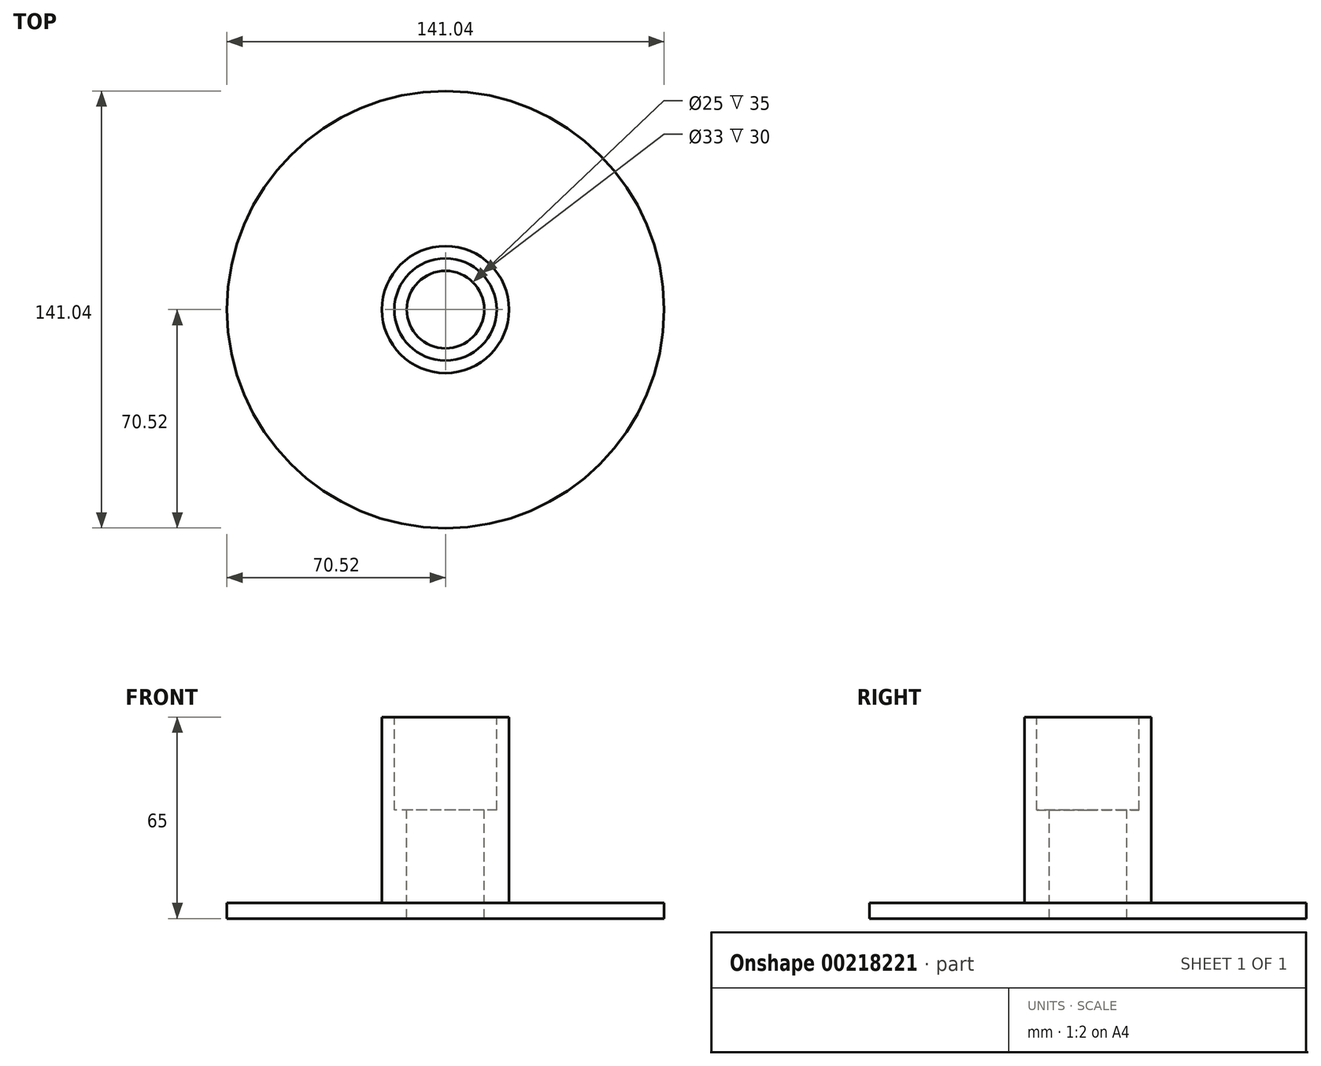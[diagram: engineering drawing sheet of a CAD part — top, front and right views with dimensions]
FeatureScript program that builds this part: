
annotation { "Feature Type Name" : "Feature", "Feature Type Description" : "" }
export const myFeature = defineFeature(function(context is Context, id is Id, definition is map)
    precondition{}
    {
        {
            var Q0;
            Q0=qCreatedBy(makeId("Front.planeOp"),FACE);
            var sketch = newSketch(context, id + "F0", { "sketchPlane" : qUnion([Q0])});
            skLineSegment(sketch, "E0.bottom", {"start": v(71.48, 6.77) * mm, "end": v(-70.52, 6.77) * mm});
            skLineSegment(sketch, "E0.top", {"start": v(71.48, 1.77) * mm, "end": v(-70.52, 1.77) * mm});
            skLineSegment(sketch, "E0.left", {"start": v(71.48, 6.77) * mm, "end": v(71.48, 1.77) * mm});
            skLineSegment(sketch, "E0.right", {"start": v(-70.52, 6.77) * mm, "end": v(-70.52, 1.77) * mm});
            skLineSegment(sketch, "E1.top", {"start": v(20.5, 66.77) * mm, "end": v(-20.5, 66.77) * mm});
            skLineSegment(sketch, "E1.left", {"start": v(20.5, 6.77) * mm, "end": v(20.5, 66.77) * mm});
            skLineSegment(sketch, "E1.right", {"start": v(-20.5, 6.77) * mm, "end": v(-20.5, 66.77) * mm});
            skPoint(sketch, "E1.middle", {"position": v(0, 36.77) * mm});
            skLineSegment(sketch, "E2", {"start": v(-12.5, 66.77) * mm, "end": v(-12.5, 6.77) * mm});
            skLineSegment(sketch, "E3.MirrorCS", {"start": v(12.5, 66.77) * mm, "end": v(12.5, 6.77) * mm});
            skLineSegment(sketch, "E4", {"start": v(-16.5, 66.77) * mm, "end": v(-16.5, 36.77) * mm});
            skLineSegment(sketch, "E5", {"start": v(-16.5, 36.77) * mm, "end": v(-20.5, 36.77) * mm});
            skLineSegment(sketch, "E6.MirrorCS", {"start": v(16.5, 36.77) * mm, "end": v(20.5, 36.77) * mm});
            skLineSegment(sketch, "E7.MirrorCS", {"start": v(16.5, 66.77) * mm, "end": v(16.5, 36.77) * mm});
            skLineSegment(sketch, "E8", {"start": v(-16.5, 36.77) * mm, "end": v(-12.5, 36.77) * mm});
            skLineSegment(sketch, "E9.MirrorCS", {"start": v(16.5, 36.77) * mm, "end": v(12.5, 36.77) * mm});
            skLineSegment(sketch, "E10", {"start": v(-12.5, 6.77) * mm, "end": v(-12.5, 1.77) * mm});
            skLineSegment(sketch, "E11.MirrorCS", {"start": v(12.5, 6.77) * mm, "end": v(12.5, 1.77) * mm});
            skLineSegment(sketch, "E12", {"start": v(0, 81.08) * mm, "end": v(0, -48.61) * mm, "construction": true});
            skSolve(sketch);
        }
        {
            var Q0;
            {var subQ0=sQuery(id+"F0.wireOp",EDGE,"E0.right");Q0=makeQuery(id+"F0.imprint","IMPRINT",FACE,{"disambiguationData":[TD([[makeQuery(id+"F0.imprint","IMPRINT",EDGE,{"derivedFrom":subQ0}),1.0]])]});}
            var Q1;
            {var subQ0=sQuery(id+"F0.wireOp",EDGE,"E5");Q1=makeQuery(id+"F0.imprint","IMPRINT",FACE,{"disambiguationData":[TD([[makeQuery(id+"F0.imprint","IMPRINT",EDGE,{"derivedFrom":subQ0}),1.0]])]});}
            var Q2;
            {var subQ3=sQuery(id+"F0.wireOp",EDGE,"E4");Q2=makeQuery(id+"F0.imprint","IMPRINT",FACE,{"disambiguationData":[TD([[makeQuery(id+"F0.imprint","IMPRINT",EDGE,{"derivedFrom":subQ3}),-1.0]])]});}
            var Q3;
            Q3=sQuery(id+"F0.wireOp",EDGE,"E12");
            revolve(context, id + "F1", {"entities" : qUnion([Q0, Q1, Q2]), "axis" : qUnion([Q3]), "revolveType" : RevolveType.FULL});
        }
    });
